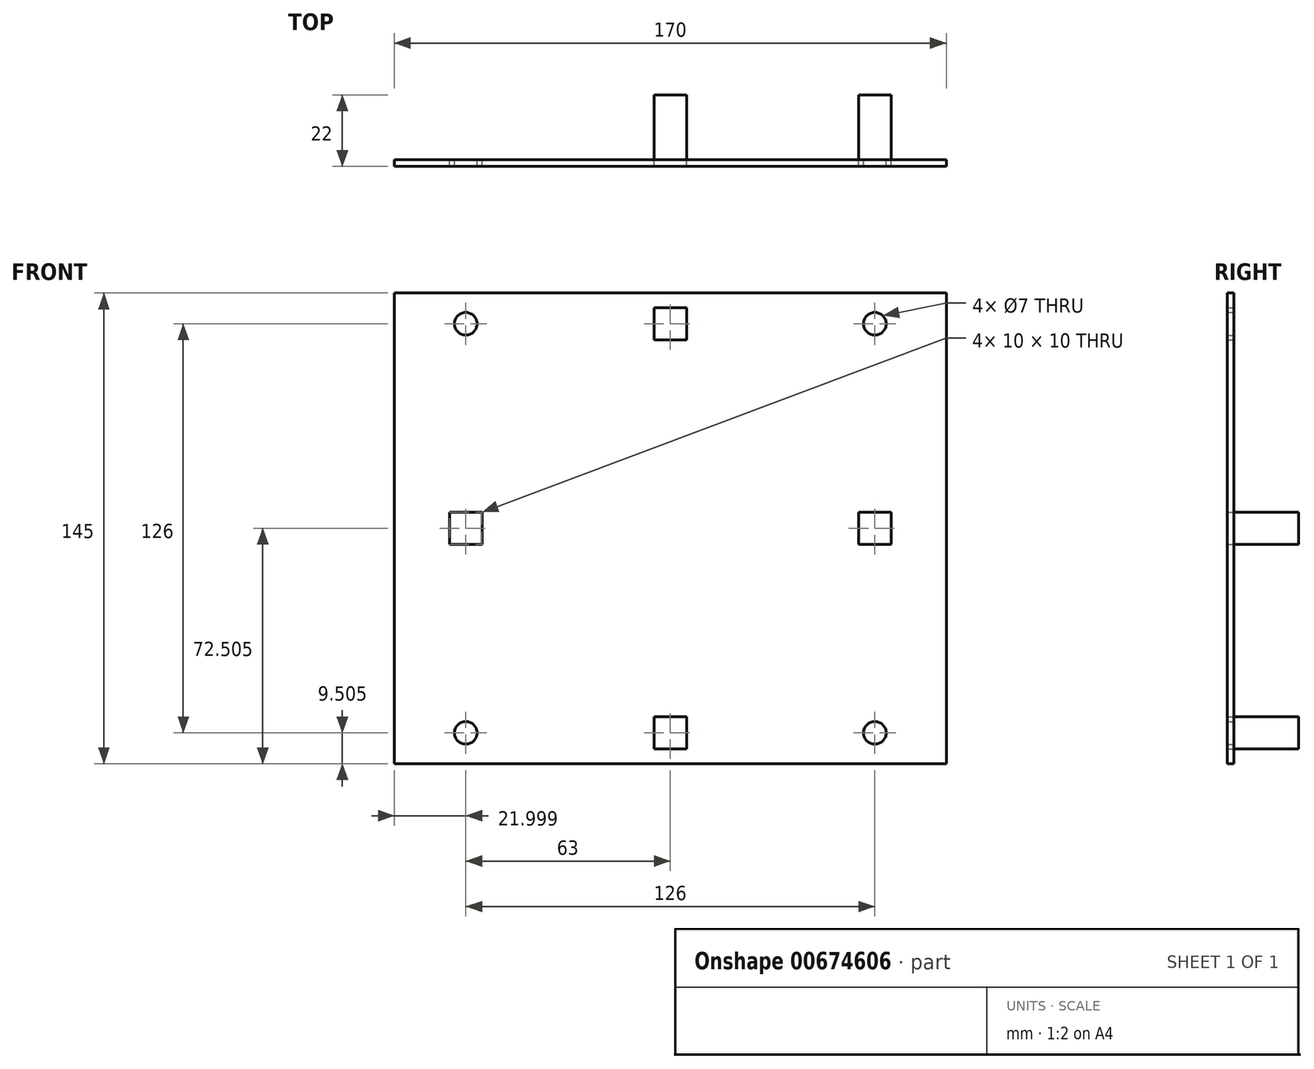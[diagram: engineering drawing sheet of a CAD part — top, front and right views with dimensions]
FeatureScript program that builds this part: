
annotation { "Feature Type Name" : "Feature", "Feature Type Description" : "" }
export const myFeature = defineFeature(function(context is Context, id is Id, definition is map)
    precondition{}
    {
        {
            var Q0;
            Q0=qCreatedBy(makeId("Front.planeOp"),FACE);
            var sketch = newSketch(context, id + "F0", { "sketchPlane" : qUnion([Q0])});
            skLineSegment(sketch, "E0.bottom", {"start": v(-113.38, 96.04) * mm, "end": v(56.62, 96.04) * mm});
            skLineSegment(sketch, "E0.top", {"start": v(-113.38, -48.96) * mm, "end": v(56.62, -48.96) * mm});
            skLineSegment(sketch, "E0.left", {"start": v(-113.38, 96.04) * mm, "end": v(-113.38, -48.96) * mm});
            skLineSegment(sketch, "E0.right", {"start": v(56.62, 96.04) * mm, "end": v(56.62, -48.96) * mm});
            skLineSegment(sketch, "E1.bottom", {"start": v(-33.38, 91.54) * mm, "end": v(-23.38, 91.54) * mm});
            skLineSegment(sketch, "E1.top", {"start": v(-33.38, 81.54) * mm, "end": v(-23.38, 81.54) * mm});
            skLineSegment(sketch, "E1.left", {"start": v(-33.38, 91.54) * mm, "end": v(-33.38, 81.54) * mm});
            skLineSegment(sketch, "E1.right", {"start": v(-23.38, 91.54) * mm, "end": v(-23.38, 81.54) * mm});
            skCircle(sketch, "E2", {"center": v(-91.38, 86.54) * mm, "radius": 3 * mm});
            skCircle(sketch, "E3", {"center": v(-91.38, 86.54) * mm, "radius": 3.5 * mm});
            skPoint(sketch, "E4.startSnap0", {"position": v(56.62, 23.54) * mm});
            skLineSegment(sketch, "E5.MirrorCS", {"start": v(-23.38, -44.46) * mm, "end": v(-23.38, -34.46) * mm});
            skLineSegment(sketch, "E6.MirrorCS", {"start": v(-33.38, -44.46) * mm, "end": v(-33.38, -34.46) * mm});
            skLineSegment(sketch, "E7.MirrorCS", {"start": v(-33.38, -34.46) * mm, "end": v(-23.38, -34.46) * mm});
            skLineSegment(sketch, "E8.MirrorCS", {"start": v(-33.38, -44.46) * mm, "end": v(-23.38, -44.46) * mm});
            skCircle(sketch, "E9.MirrorC", {"center": v(-91.38, -39.46) * mm, "radius": 3 * mm});
            skCircle(sketch, "E10.MirrorC", {"center": v(-91.38, -39.46) * mm, "radius": 3.5 * mm});
            skCircle(sketch, "E11.MirrorC", {"center": v(34.62, 86.54) * mm, "radius": 3.5 * mm});
            skCircle(sketch, "E12.MirrorC", {"center": v(34.62, 86.54) * mm, "radius": 3 * mm});
            skCircle(sketch, "E13.MirrorC", {"center": v(34.62, -39.46) * mm, "radius": 3.5 * mm});
            skCircle(sketch, "E14.MirrorC", {"center": v(34.62, -39.46) * mm, "radius": 3 * mm});
            skLineSegment(sketch, "E15.bottom", {"start": v(-96.38, 28.54) * mm, "end": v(-86.38, 28.54) * mm});
            skLineSegment(sketch, "E15.top", {"start": v(-96.38, 18.54) * mm, "end": v(-86.38, 18.54) * mm});
            skLineSegment(sketch, "E15.left", {"start": v(-96.38, 28.54) * mm, "end": v(-96.38, 18.54) * mm});
            skLineSegment(sketch, "E15.right", {"start": v(-86.38, 28.54) * mm, "end": v(-86.38, 18.54) * mm});
            skLineSegment(sketch, "E16.MirrorCS", {"start": v(39.62, 18.54) * mm, "end": v(29.62, 18.54) * mm});
            skLineSegment(sketch, "E17.MirrorCS", {"start": v(29.62, 28.54) * mm, "end": v(29.62, 18.54) * mm});
            skLineSegment(sketch, "E18.MirrorCS", {"start": v(39.62, 28.54) * mm, "end": v(39.62, 18.54) * mm});
            skLineSegment(sketch, "E19.MirrorCS", {"start": v(39.62, 28.54) * mm, "end": v(29.62, 28.54) * mm});
            skSolve(sketch);
        }
        {
            var Q0;
            Q0=makeQuery(id+"F0.imprint","IMPRINT",FACE,{"disambiguationData":[TD([[makeQuery(id+"F0.imprint","IMPRINT",EDGE,{"derivedFrom":sQuery(id+"F0.wireOp",EDGE,"E12.MirrorC")}),-1.0]])]});
            var Q1;
            Q1=sQuery(id+"F0.wireOp",EDGE,"E3");
            extrude(context, id + "F1", {"entities" : qUnion([Q0]), "bodyType" : ToolBodyType.SURFACE, "surfaceEntities" : qUnion([Q1]), "oppositeDirection" : true, "depth" : 33 * mm, "offsetDistance" : 25 * mm});
        }
        {
            var Q0;
            Q0=sQuery(id+"F0.wireOp",EDGE,"E9.MirrorC");
            extrude(context, id + "F2", {"bodyType" : ToolBodyType.SURFACE, "surfaceEntities" : qUnion([Q0]), "oppositeDirection" : true, "depth" : 33 * mm, "offsetDistance" : 25 * mm});
        }
        {
            var Q0;
            Q0=makeQuery(id+"F0.imprint","IMPRINT",FACE,{"disambiguationData":[TD([[makeQuery(id+"F0.imprint","IMPRINT",EDGE,{"derivedFrom":sQuery(id+"F0.wireOp",EDGE,"E0.bottom")}),-1.0]])]});
            var Q1;
            Q1=sQuery(id+"F0.wireOp",EDGE,"E14.MirrorC");
            extrude(context, id + "F3", {"entities" : qUnion([Q0]), "bodyType" : ToolBodyType.SURFACE, "surfaceEntities" : qUnion([Q1]), "oppositeDirection" : true, "depth" : 33 * mm, "offsetDistance" : 25 * mm});
        }
        {
            var Q0;
            Q0=sQuery(id+"F0.wireOp",EDGE,"E11.MirrorC");
            extrude(context, id + "F4", {"bodyType" : ToolBodyType.SURFACE, "surfaceEntities" : qUnion([Q0]), "oppositeDirection" : true, "depth" : 33 * mm, "offsetDistance" : 25 * mm});
        }
        {
            var Q0;
            Q0=sQuery(id+"F0.wireOp",EDGE,"E15.right");
            var Q1;
            Q1=sQuery(id+"F0.wireOp",EDGE,"E15.bottom");
            var Q2;
            Q2=sQuery(id+"F0.wireOp",EDGE,"E15.left");
            var Q3;
            Q3=sQuery(id+"F0.wireOp",EDGE,"E15.top");
            extrude(context, id + "F5", {"bodyType" : ToolBodyType.SURFACE, "surfaceEntities" : qUnion([Q0, Q1, Q2, Q3]), "oppositeDirection" : true, "depth" : 20 * mm, "offsetDistance" : 25 * mm});
        }
        {
            var Q0;
            Q0=sQuery(id+"F0.wireOp",EDGE,"E1.top");
            var Q1;
            Q1=sQuery(id+"F0.wireOp",EDGE,"E1.bottom");
            var Q2;
            Q2=sQuery(id+"F0.wireOp",EDGE,"E1.right");
            var Q3;
            Q3=sQuery(id+"F0.wireOp",EDGE,"E1.left");
            extrude(context, id + "F6", {"bodyType" : ToolBodyType.SURFACE, "surfaceEntities" : qUnion([Q0, Q1, Q2, Q3]), "oppositeDirection" : true, "depth" : 20 * mm, "offsetDistance" : 25 * mm});
        }
        {
            var Q0;
            Q0=makeQuery(id+"F0.imprint","IMPRINT",FACE,{"disambiguationData":[TD([[makeQuery(id+"F0.imprint","IMPRINT",EDGE,{"derivedFrom":sQuery(id+"F0.wireOp",EDGE,"E16.MirrorCS")}),-1.0]])]});
            extrude(context, id + "F7", {"entities" : qUnion([Q0]), "oppositeDirection" : true, "depth" : 20 * mm, "offsetDistance" : 25 * mm});
        }
        {
            var Q0;
            Q0=makeQuery(id+"F0.imprint","IMPRINT",FACE,{"disambiguationData":[TD([[makeQuery(id+"F0.imprint","IMPRINT",EDGE,{"derivedFrom":sQuery(id+"F0.wireOp",EDGE,"E5.MirrorCS")}),1.0]])]});
            extrude(context, id + "F8", {"entities" : qUnion([Q0]), "oppositeDirection" : true, "depth" : 20 * mm, "offsetDistance" : 25 * mm});
        }
        {
            var Q0;
            Q0=makeQuery(id+"F0.imprint","IMPRINT",FACE,{"disambiguationData":[TD([[makeQuery(id+"F0.imprint","IMPRINT",EDGE,{"derivedFrom":sQuery(id+"F0.wireOp",EDGE,"E0.bottom")}),-1.0]])]});
            extrude(context, id + "F9", {"entities" : qUnion([Q0]), "depth" : 2 * mm, "offsetDistance" : 25 * mm});
        }
    });
